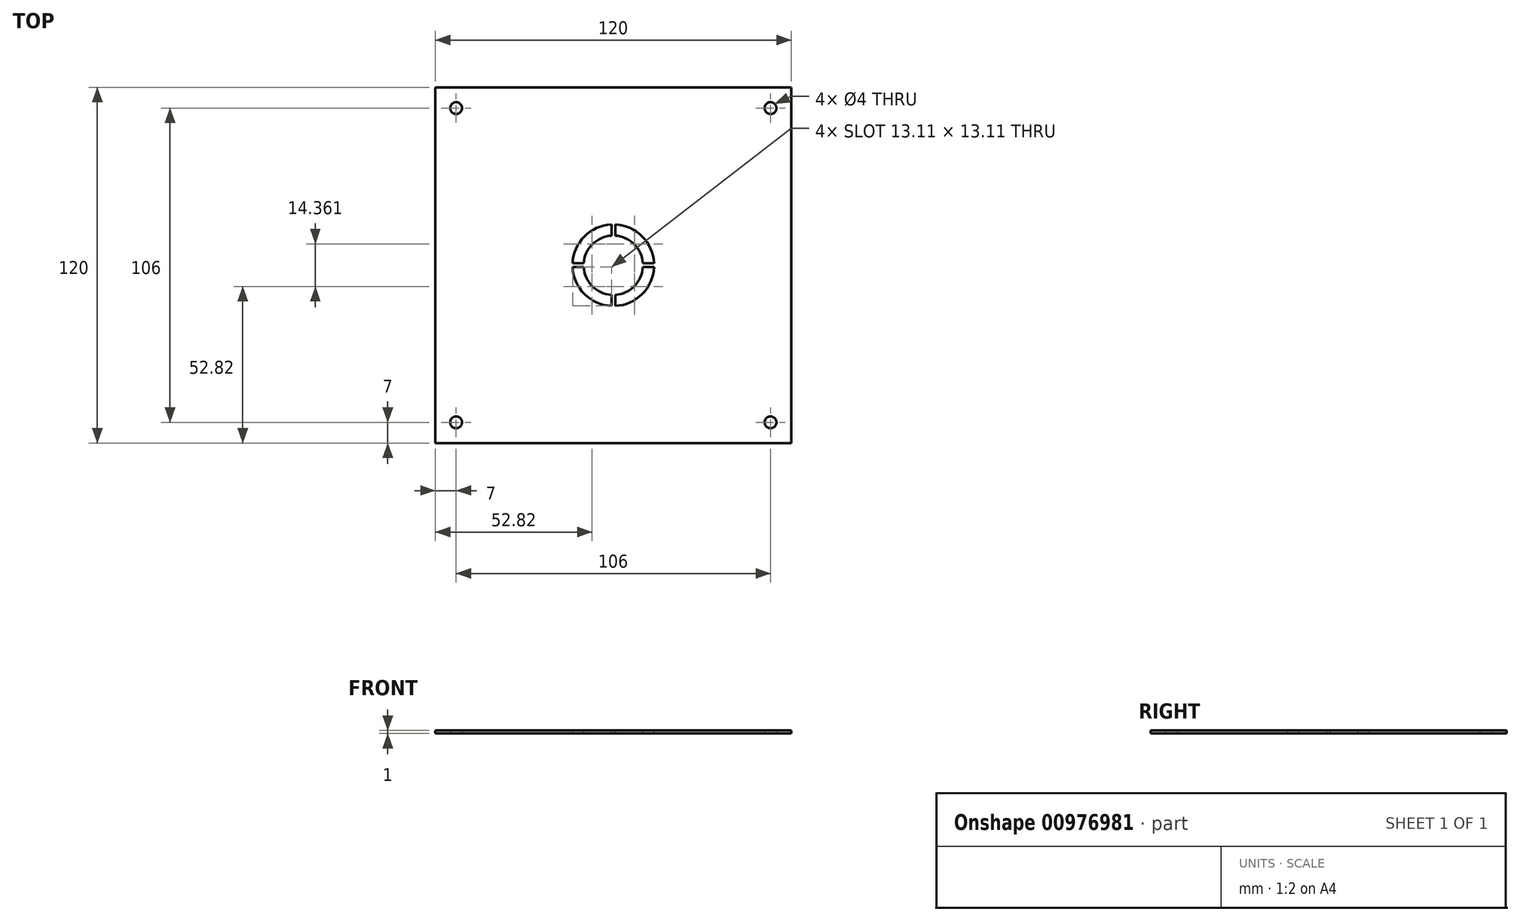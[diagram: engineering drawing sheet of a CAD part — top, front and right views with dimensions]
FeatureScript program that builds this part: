
annotation { "Feature Type Name" : "Feature", "Feature Type Description" : "" }
export const myFeature = defineFeature(function(context is Context, id is Id, definition is map)
    precondition{}
    {
        {
            assignVariable(context, id + "F0", {"name" : "inc", "anyValue" : 10});
        }
        {
            assignVariable(context, id + "F1", {"name" : "diam", "anyValue" : 10});
        }
        {
            assignVariable(context, id + "F2", {"name" : "diam", "anyValue" : getVariable(context, 'diam') + getVariable(context, 'inc')});
        }
        {
            var Q0;
            Q0=qCreatedBy(makeId("Top.planeOp"),FACE);
            var sketch = newSketch(context, id + "F3", { "sketchPlane" : qUnion([Q0]), "disableImprinting" : false});
            skLineSegment(sketch, "E0.bottom", {"start": v(60, 60) * mm, "end": v(-60, 60) * mm});
            skLineSegment(sketch, "E0.top", {"start": v(60, -60) * mm, "end": v(-60, -60) * mm});
            skLineSegment(sketch, "E0.left", {"start": v(60, 60) * mm, "end": v(60, -60) * mm});
            skLineSegment(sketch, "E0.right", {"start": v(-60, 60) * mm, "end": v(-60, -60) * mm});
            skPoint(sketch, "E0.middle", {"position": v(0, 0) * mm});
            skCircle(sketch, "E1", {"center": v(0, 0) * mm, "radius": 60 * mm, "construction": true});
            skLineSegment(sketch, "E2", {"start": v(0, 60) * mm, "end": v(0, -60) * mm, "construction": true});
            skLineSegment(sketch, "E3", {"start": v(-60, 0) * mm, "end": v(60, 0) * mm, "construction": true});
            skLineSegment(sketch, "E4", {"start": v(-0.63, 60) * mm, "end": v(-0.62, -60) * mm});
            skLineSegment(sketch, "E5.MirrorCS", {"start": v(0.63, 60) * mm, "end": v(0.62, -60) * mm});
            skLineSegment(sketch, "E6", {"start": v(-60, 0.62) * mm, "end": v(60, 0.63) * mm});
            skLineSegment(sketch, "E7.MirrorCS", {"start": v(-60, -0.62) * mm, "end": v(60, -0.63) * mm});
            skCircle(sketch, "E8", {"center": v(-53, -53) * mm, "radius": 2 * mm});
            skCircle(sketch, "E9.MirrorC", {"center": v(-53, 53) * mm, "radius": 2 * mm});
            skCircle(sketch, "E10.MirrorC", {"center": v(53, 53) * mm, "radius": 2 * mm});
            skCircle(sketch, "E11.MirrorC", {"center": v(53, -53) * mm, "radius": 2 * mm});
            skSolve(sketch);
        }
        {
            var Q0;
            Q0=qSketchRegion(id+"F3",true);
            var Q1;
            {var subQ0=sQuery(id+"F3.wireOp",EDGE,"E6");var subQ1=sQuery(id+"F3.wireOp",EDGE,"E4");var subQ2=makeQuery(id+"F3.imprint","INTERSECT",VERTEX,{"derivedFrom":[subQ1,subQ0]});Q1=makeQuery(id+"F3.imprint","IMPRINT",FACE,{"disambiguationData":[TD([[makeQuery(id+"F3.imprint","IMPRINT",EDGE,{"disambiguationData":[TD([[subQ2,-1.0]])],"derivedFrom":subQ1}),1.0]])]});}
            extrude(context, id + "F4", {"entities" : qUnion([Q0, Q1]), "flatOperationType" : FlatOperationType.REMOVE, "offsetDistance" : 25 * mm, "depth" : 1 * mm, "domain" : OperationDomain.MODEL});
        }
        {
            var Q0;
            Q0=makeQuery(id+"F4.opExtrude","CAP_FACE",FACE,{"disambiguationData":[OSD([sQuery(id+"F3.wireOp",EDGE,"E0.bottom"),sQuery(id+"F3.wireOp",EDGE,"E0.top"),sQuery(id+"F3.wireOp",EDGE,"E0.left"),sQuery(id+"F3.wireOp",EDGE,"E0.right")])],"isStart":false});
            var sketch = newSketch(context, id + "F5", { "sketchPlane" : qUnion([Q0])});
            skCircle(sketch, "E12", {"center": v(0, 0) * mm, "radius": 10 * mm});
            skCircle(sketch, "E13", {"center": v(0, 0) * mm, "radius": 13.75 * mm});
            skSolve(sketch);
        }
        {
            var Q0;
            Q0=makeQuery(id+"F5.imprint","IMPRINT",FACE,{"disambiguationData":[TD([[makeQuery(id+"F5.imprint","IMPRINT",EDGE,{"derivedFrom":sQuery(id+"F5.wireOp",EDGE,"E12")}),-1.0]])]});
            extrude(context, id + "F6", {"entities" : qUnion([Q0]), "operationType" : NewBodyOperationType.REMOVE, "endBound" : BoundingType.THROUGH_ALL, "oppositeDirection" : true, "depth" : 25 * mm});
        }
        {
            var Q0;
            {var subQ0=sQuery(id+"F3.wireOp",EDGE,"E6");var subQ1=sQuery(id+"F3.wireOp",EDGE,"E0.right");var subQ2=makeQuery(id+"F3.imprint","INTERSECT",VERTEX,{"derivedFrom":[subQ1,subQ0]});Q0=makeQuery(id+"F3.imprint","IMPRINT",FACE,{"disambiguationData":[TD([[makeQuery(id+"F3.imprint","IMPRINT",EDGE,{"disambiguationData":[TD([[subQ2,-1.0]])],"derivedFrom":subQ1}),1.0]])]});}
            var Q1;
            {var subQ0=sQuery(id+"F3.wireOp",EDGE,"E6");var subQ1=sQuery(id+"F3.wireOp",EDGE,"E4");var subQ2=makeQuery(id+"F3.imprint","INTERSECT",VERTEX,{"derivedFrom":[subQ1,subQ0]});Q1=makeQuery(id+"F3.imprint","IMPRINT",FACE,{"disambiguationData":[TD([[makeQuery(id+"F3.imprint","IMPRINT",EDGE,{"disambiguationData":[TD([[subQ2,-1.0]])],"derivedFrom":subQ1}),1.0]])]});}
            var Q2;
            {var subQ0=sQuery(id+"F3.wireOp",EDGE,"E4");var subQ1=sQuery(id+"F3.wireOp",EDGE,"E0.bottom");var subQ2=makeQuery(id+"F3.imprint","INTERSECT",VERTEX,{"derivedFrom":[subQ1,subQ0]});Q2=makeQuery(id+"F3.imprint","IMPRINT",FACE,{"disambiguationData":[TD([[makeQuery(id+"F3.imprint","IMPRINT",EDGE,{"disambiguationData":[TD([[subQ2,1.0]])],"derivedFrom":subQ1}),1.0]])]});}
            var Q3;
            {var subQ0=sQuery(id+"F3.wireOp",EDGE,"E6");var subQ1=sQuery(id+"F3.wireOp",EDGE,"E0.left");var subQ2=makeQuery(id+"F3.imprint","INTERSECT",VERTEX,{"derivedFrom":[subQ1,subQ0]});Q3=makeQuery(id+"F3.imprint","IMPRINT",FACE,{"disambiguationData":[TD([[makeQuery(id+"F3.imprint","IMPRINT",EDGE,{"disambiguationData":[TD([[subQ2,-1.0]])],"derivedFrom":subQ1}),-1.0]])]});}
            var Q4;
            {var subQ0=sQuery(id+"F3.wireOp",EDGE,"E4");var subQ1=sQuery(id+"F3.wireOp",EDGE,"E0.top");var subQ2=makeQuery(id+"F3.imprint","INTERSECT",VERTEX,{"derivedFrom":[subQ1,subQ0]});Q4=makeQuery(id+"F3.imprint","IMPRINT",FACE,{"disambiguationData":[TD([[makeQuery(id+"F3.imprint","IMPRINT",EDGE,{"disambiguationData":[TD([[subQ2,1.0]])],"derivedFrom":subQ1}),-1.0]])]});}
            extrude(context, id + "F7", {"entities" : qUnion([Q0, Q1, Q2, Q3, Q4]), "operationType" : NewBodyOperationType.ADD, "depth" : 1 * mm});
        }
    });
